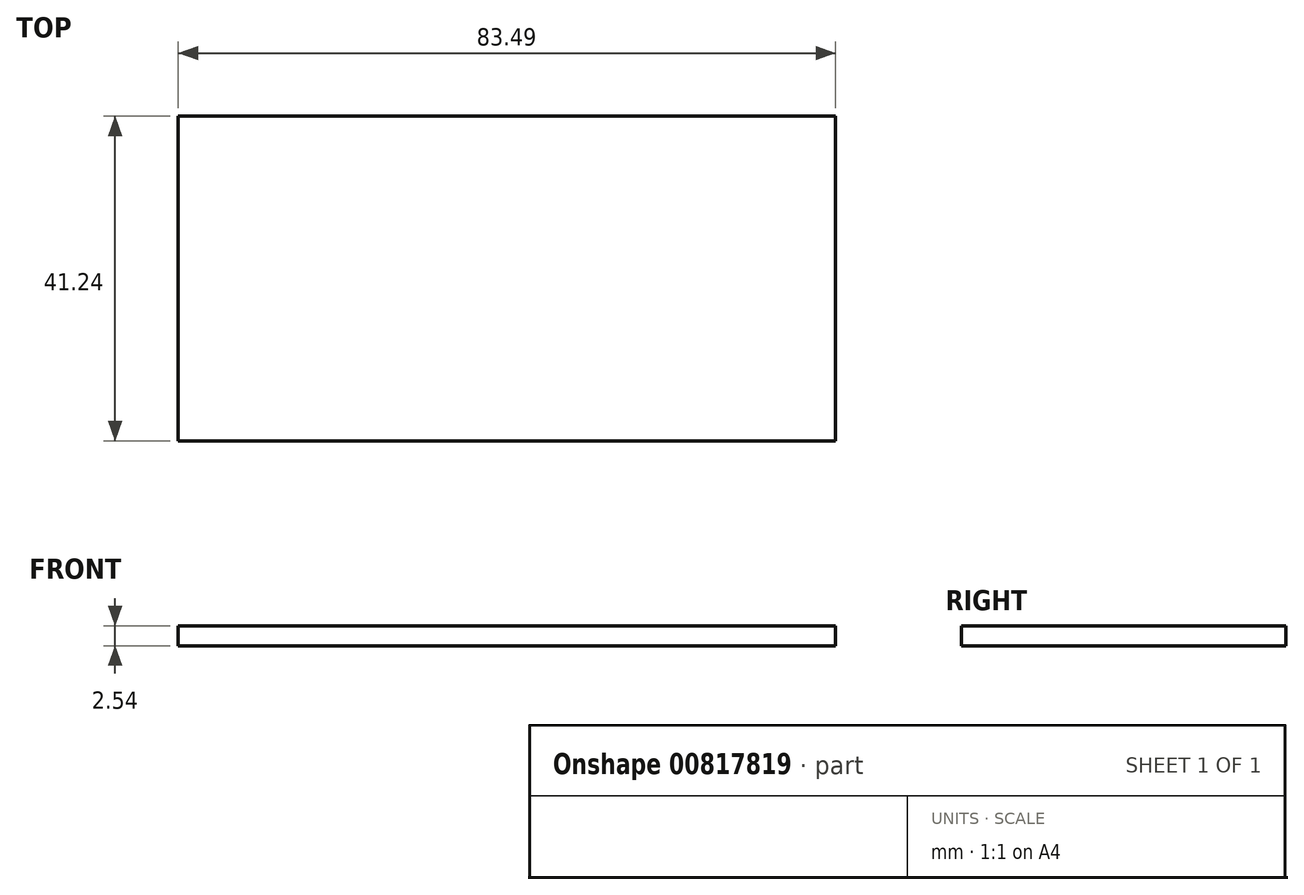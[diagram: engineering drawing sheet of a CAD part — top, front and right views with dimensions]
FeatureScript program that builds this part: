
annotation { "Feature Type Name" : "Feature", "Feature Type Description" : "" }
export const myFeature = defineFeature(function(context is Context, id is Id, definition is map)
    precondition{}
    {
        {
            var Q0;
            Q0=qCreatedBy(makeId("Top.planeOp"),FACE);
            var sketch = newSketch(context, id + "F0", { "sketchPlane" : qUnion([Q0])});
            skLineSegment(sketch, "E0.bottom", {"start": v(-30.72, -21.35) * mm, "end": v(52.9, -21.35) * mm});
            skLineSegment(sketch, "E0.top", {"start": v(-30.72, 19.47) * mm, "end": v(52.9, 19.47) * mm});
            skLineSegment(sketch, "E0.left", {"start": v(-30.72, -21.35) * mm, "end": v(-30.72, 19.47) * mm});
            skLineSegment(sketch, "E0.right", {"start": v(52.9, -21.35) * mm, "end": v(52.9, 19.47) * mm});
            skText(sketch, "E1", { "text": "Emily", "fontName": "RobotoSlab-Bold.ttf"});
            const initialGuessF0  = {"E1": [-0.01635, -0.00758, 1, 0, 0.01396]};
            skSetInitialGuess(sketch, initialGuessF0);
            skSolve(sketch);
        }
        {
            var Q0;
            Q0=makeQuery(id+"F0.imprint","IMPRINT",FACE,{"disambiguationData":[TD([[makeQuery(id+"F0.imprint","IMPRINT",EDGE,{"derivedFrom":sQuery(id+"F0.wireOp",EDGE,"E0.bottom")}),1.0]])]});
            var sketch = newSketch(context, id + "F1", { "sketchPlane" : qUnion([Q0])});
            skLineSegment(sketch, "E2.bottom", {"start": v(-30.61, 19.62) * mm, "end": v(52.88, 19.62) * mm});
            skLineSegment(sketch, "E2.top", {"start": v(-30.61, -21.62) * mm, "end": v(52.88, -21.62) * mm});
            skLineSegment(sketch, "E2.left", {"start": v(-30.61, 19.62) * mm, "end": v(-30.61, -21.62) * mm});
            skLineSegment(sketch, "E2.right", {"start": v(52.88, 19.62) * mm, "end": v(52.88, -21.62) * mm});
            skSolve(sketch);
        }
        {
            var Q0;
            Q0 = qSketchRegion(id + "F1", true);
            extrude(context, id + "F2", {"entities" : qUnion([Q0]), "depth" : 0 * mm, "offsetDistance" : 25.4 * mm, "hasSecondDirection" : true, "secondDirectionOppositeDirection" : true, "secondDirectionDepth" : 2.54 * mm});
        }
    });
